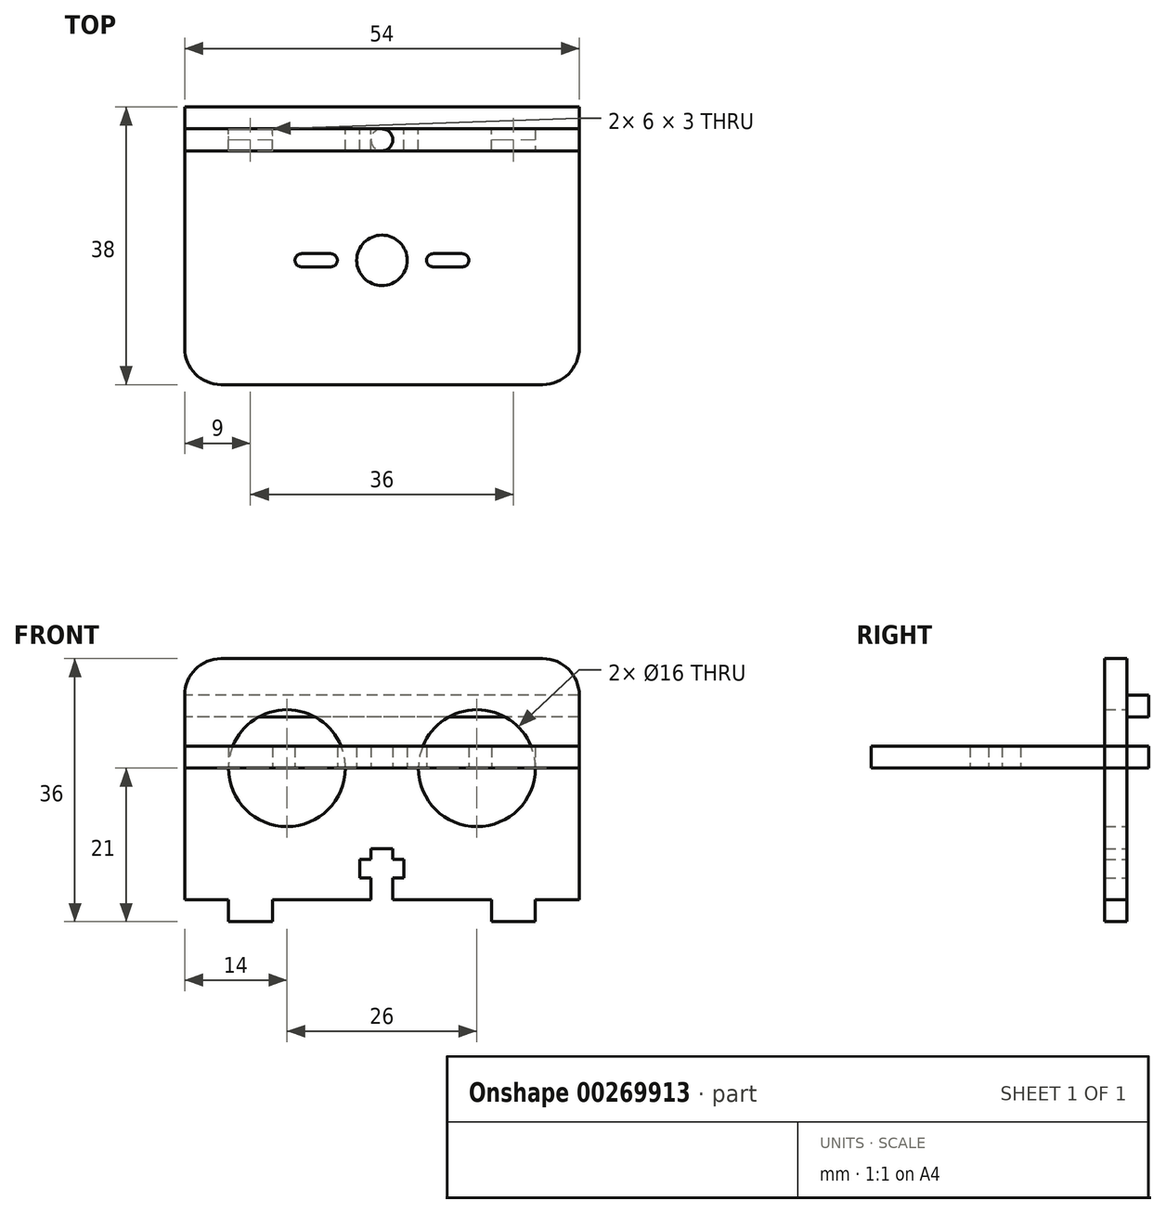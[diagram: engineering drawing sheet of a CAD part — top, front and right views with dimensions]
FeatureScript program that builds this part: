
annotation { "Feature Type Name" : "Feature", "Feature Type Description" : "" }
export const myFeature = defineFeature(function(context is Context, id is Id, definition is map)
    precondition{}
    {
        {
            var Q0;
            Q0=qCreatedBy(makeId("Front.planeOp"),FACE);
            var sketch = newSketch(context, id + "F0", { "sketchPlane" : qUnion([Q0])});
            skLineSegment(sketch, "E0.bottom", {"start": v(-22, 15) * mm, "end": v(22, 15) * mm});
            skLineSegment(sketch, "E0.left", {"start": v(-27, 10) * mm, "end": v(-27, -15) * mm});
            skLineSegment(sketch, "E0.right", {"start": v(27, 10) * mm, "end": v(27, -15) * mm});
            skCircle(sketch, "E1", {"center": v(13, 0) * mm, "radius": 8 * mm});
            skCircle(sketch, "E2", {"center": v(-13, 0) * mm, "radius": 8 * mm});
            skLineSegment(sketch, "E3", {"start": v(-36.52, -18) * mm, "end": v(-21, -18) * mm, "construction": true});
            skLineSegment(sketch, "E4", {"start": v(-9, -18) * mm, "end": v(-3, -18) * mm});
            skLineSegment(sketch, "E5", {"start": v(-3, -15) * mm, "end": v(-1.5, -15) * mm});
            skLineSegment(sketch, "E6", {"start": v(3, -18) * mm, "end": v(9, -18) * mm});
            skPoint(sketch, "E7.oppositeSnap0", {"position": v(1.5, -18) * mm});
            skLineSegment(sketch, "E7.bottom", {"start": v(0, -18) * mm, "end": v(1.5, -18) * mm});
            skLineSegment(sketch, "E7.top", {"start": v(0, -11) * mm, "end": v(1.5, -11) * mm});
            skLineSegment(sketch, "E7.right", {"start": v(1.5, -18) * mm, "end": v(1.5, -15) * mm});
            skLineSegment(sketch, "E8.trimOffspring", {"start": v(1.5, -18) * mm, "end": v(9, -18) * mm, "construction": true});
            skLineSegment(sketch, "E9", {"start": v(3, -18) * mm, "end": v(1.5, -18) * mm});
            skLineSegment(sketch, "E10.top", {"start": v(-3, -12.5) * mm, "end": v(-1.5, -12.5) * mm});
            skLineSegment(sketch, "E10.left", {"start": v(-3, -15) * mm, "end": v(-3, -12.5) * mm});
            skLineSegment(sketch, "E10.right", {"start": v(3, -15) * mm, "end": v(3, -12.5) * mm});
            skLineSegment(sketch, "E11.trimOffspring", {"start": v(1.5, -15) * mm, "end": v(3, -15) * mm});
            skLineSegment(sketch, "E12.trimOffspring", {"start": v(1.5, -12.5) * mm, "end": v(3, -12.5) * mm});
            skLineSegment(sketch, "E13", {"start": v(0, -11) * mm, "end": v(-1.5, -11) * mm});
            skLineSegment(sketch, "E14", {"start": v(-1.5, -11) * mm, "end": v(-1.5, -12.5) * mm});
            skLineSegment(sketch, "E15.trimOffspring", {"start": v(1.5, -12.5) * mm, "end": v(1.5, -11) * mm});
            skLineSegment(sketch, "E16.trimOffspring", {"start": v(-1.5, -15) * mm, "end": v(-1.5, -18) * mm});
            skLineSegment(sketch, "E17", {"start": v(-1.5, -18) * mm, "end": v(-3, -18) * mm});
            skLineSegment(sketch, "E18", {"start": v(-21, -18) * mm, "end": v(-21, -21) * mm});
            skLineSegment(sketch, "E19", {"start": v(-21, -21) * mm, "end": v(-15, -21) * mm});
            skLineSegment(sketch, "E20", {"start": v(-15, -21) * mm, "end": v(-15, -18) * mm});
            skLineSegment(sketch, "E21", {"start": v(-15, -18) * mm, "end": v(-9, -18) * mm});
            skLineSegment(sketch, "E22", {"start": v(9, -18) * mm, "end": v(15, -18) * mm});
            skLineSegment(sketch, "E23", {"start": v(15, -18) * mm, "end": v(15, -21) * mm});
            skLineSegment(sketch, "E24", {"start": v(15, -21) * mm, "end": v(21, -21) * mm});
            skLineSegment(sketch, "E25", {"start": v(21, -21) * mm, "end": v(21, -18) * mm});
            skLineSegment(sketch, "E26.trimOffspring", {"start": v(-15, -18) * mm, "end": v(0, -18) * mm, "construction": true});
            skLineSegment(sketch, "E27.trimOffspring", {"start": v(21, -18) * mm, "end": v(39.52, -18) * mm, "construction": true});
            skPoint(sketch, "E28.visualSharp", {"position": v(-27, 15) * mm});
            skArc(sketch, "E28.filletArc", {"start": v(-22, 15) * mm, "mid": v(-25.54, 13.54) * mm, "end": v(-27, 10) * mm});
            skPoint(sketch, "E29.visualSharp", {"position": v(27, 15) * mm});
            skArc(sketch, "E29.filletArc", {"start": v(27, 10) * mm, "mid": v(25.54, 13.54) * mm, "end": v(22, 15) * mm});
            skLineSegment(sketch, "E30", {"start": v(-27, -15) * mm, "end": v(-27, -18) * mm});
            skLineSegment(sketch, "E31", {"start": v(-27, -18) * mm, "end": v(-21, -18) * mm});
            skPoint(sketch, "E32.start.orphan", {"position": v(-21, -15) * mm});
            skLineSegment(sketch, "E33", {"start": v(27, -15) * mm, "end": v(27, -18) * mm});
            skLineSegment(sketch, "E34", {"start": v(27, -18) * mm, "end": v(21, -18) * mm});
            skSolve(sketch);
        }
        {
            var Q0;
            Q0=makeQuery(id+"F0.imprint","IMPRINT",FACE,{"disambiguationData":[TD([[makeQuery(id+"F0.imprint","IMPRINT",EDGE,{"derivedFrom":sQuery(id+"F0.wireOp",EDGE,"E0.bottom")}),-1.0]])]});
            var Q1;
            {var subQ0=sQuery(id+"F0.wireOp",EDGE,"E32");Q1=makeQuery(id+"F0.imprint","IMPRINT",FACE,{"disambiguationData":[TD([[makeQuery(id+"F0.imprint","IMPRINT",EDGE,{"derivedFrom":subQ0}),1.0]])]});}
            var Q2;
            {var subQ0=sQuery(id+"F0.wireOp",EDGE,"chz3AYh3-IsNQ-ujgV-jPsD-pE5skbg77R1T");Q2=makeQuery(id+"F0.imprint","IMPRINT",FACE,{"disambiguationData":[TD([[makeQuery(id+"F0.imprint","IMPRINT",EDGE,{"derivedFrom":subQ0}),1.0]])]});}
            var Q3;
            {var subQ0=sQuery(id+"F0.wireOp",EDGE,"wKKlznAo-Ev7Z-Zq9Q-11uT-MNoMT551QMHz");Q3=makeQuery(id+"F0.imprint","IMPRINT",FACE,{"disambiguationData":[TD([[makeQuery(id+"F0.imprint","IMPRINT",EDGE,{"derivedFrom":subQ0}),1.0]])]});}
            var Q4;
            {var subQ0=sQuery(id+"F0.wireOp",EDGE,"eYgF27Q2-r109-4hkZ-zSBN-Yc0fYFjueZed");Q4=makeQuery(id+"F0.imprint","IMPRINT",FACE,{"disambiguationData":[TD([[makeQuery(id+"F0.imprint","IMPRINT",EDGE,{"derivedFrom":subQ0}),1.0]])]});}
            extrude(context, id + "F1", {"entities" : qUnion([Q0, Q1, Q2, Q3, Q4]), "depth" : 3 * mm});
        }
        {
            var Q0;
            Q0=makeQuery(id+"F1.opExtrude","CAP_FACE",FACE,{"disambiguationData":[OSD([sQuery(id+"F0.wireOp",EDGE,"E0.bottom"),sQuery(id+"F0.wireOp",EDGE,"E0.top"),sQuery(id+"F0.wireOp",EDGE,"E0.left"),sQuery(id+"F0.wireOp",EDGE,"E0.right"),sQuery(id+"F0.wireOp",EDGE,"E1"),sQuery(id+"F0.wireOp",EDGE,"E2"),sQuery(id+"F0.wireOp",EDGE,"E32"),sQuery(id+"F0.wireOp",EDGE,"YojEBUgW-nhLJ-40ki-FCGF-5mKsaDnZTmev"),sQuery(id+"F0.wireOp",EDGE,"vRN4Y9O1-ZqiY-Jczt-QRZo-3q2dczrKPTGp"),sQuery(id+"F0.wireOp",EDGE,"zzXZZM5g-6FFm-bmIo-3Ds1-M5u7KWrwiJGG"),sQuery(id+"F0.wireOp",EDGE,"chz3AYh3-IsNQ-ujgV-jPsD-pE5skbg77R1T"),sQuery(id+"F0.wireOp",EDGE,"E4"),sQuery(id+"F0.wireOp",EDGE,"ghqL6N1V-hfz9-jjIh-pt2L-dAo4biIIS88P"),sQuery(id+"F0.wireOp",EDGE,"E5"),sQuery(id+"F0.wireOp",EDGE,"wKKlznAo-Ev7Z-Zq9Q-11uT-MNoMT551QMHz"),sQuery(id+"F0.wireOp",EDGE,"E6"),sQuery(id+"F0.wireOp",EDGE,"I0ca3B4m-FfYs-K0F9-6d8p-SOPzohqiJkWk"),sQuery(id+"F0.wireOp",EDGE,"1psEPeUv-bJOJ-tgm4-QE24-8bz3CrIUmwqz"),sQuery(id+"F0.wireOp",EDGE,"eYgF27Q2-r109-4hkZ-zSBN-Yc0fYFjueZed"),sQuery(id+"F0.wireOp",EDGE,"Y0FXYbVY-FO2c-i97v-nV3U-BxFzxJudH6SC"),sQuery(id+"F0.wireOp",EDGE,"8HbA60u2-9wGZ-Dvxy-T3Xx-RcAAK77T48SR")])],"isStart":true});
            var sketch = newSketch(context, id + "F2", { "sketchPlane" : qUnion([Q0])});
            skLineSegment(sketch, "E35.bottom", {"start": v(-27, 10) * mm, "end": v(27, 10) * mm});
            skLineSegment(sketch, "E35.top", {"start": v(-27, 7) * mm, "end": v(27, 7) * mm});
            skLineSegment(sketch, "E35.left", {"start": v(-27, 10) * mm, "end": v(-27, 7) * mm});
            skLineSegment(sketch, "E35.right", {"start": v(27, 10) * mm, "end": v(27, 7) * mm});
            skSolve(sketch);
        }
        {
            var Q0;
            Q0 = qSketchRegion(id + "F2", true);
            extrude(context, id + "F3", {"entities" : qUnion([Q0]), "depth" : 3 * mm, "offsetDistance" : 25 * mm});
        }
        {
            var Q0;
            Q0=qCreatedBy(makeId("Top.planeOp"),FACE);
            var sketch = newSketch(context, id + "F4", { "sketchPlane" : qUnion([Q0])});
            skLineSegment(sketch, "E36.0", {"start": v(-27, -3) * mm, "end": v(-27, 0) * mm});
            skLineSegment(sketch, "E37.0", {"start": v(27, 0) * mm, "end": v(27, -3) * mm});
            skLineSegment(sketch, "E38.top", {"start": v(-21, 0) * mm, "end": v(-15, 0) * mm});
            skLineSegment(sketch, "E38.left", {"start": v(-27, 0) * mm, "end": v(-27, 0) * mm});
            skLineSegment(sketch, "E38.right", {"start": v(27, 0) * mm, "end": v(27, 0) * mm});
            skLineSegment(sketch, "E39.top", {"start": v(-22, -35) * mm, "end": v(22, -35) * mm});
            skLineSegment(sketch, "E39.left", {"start": v(-27, 0) * mm, "end": v(-27, -30) * mm});
            skLineSegment(sketch, "E39.right", {"start": v(27, 0) * mm, "end": v(27, -30) * mm});
            skLineSegment(sketch, "E40", {"start": v(-29.98, -1.5) * mm, "end": v(31.4, -1.5) * mm, "construction": true});
            skCircle(sketch, "E41", {"center": v(0, -1.5) * mm, "radius": 1.5 * mm});
            skLineSegment(sketch, "E42", {"start": v(-27, -3) * mm, "end": v(27, -3) * mm, "construction": true});
            skLineSegment(sketch, "E43.0", {"start": v(-21, -3) * mm, "end": v(-21, 0) * mm});
            skLineSegment(sketch, "E44.0", {"start": v(-15, -3) * mm, "end": v(-15, 0) * mm});
            skLineSegment(sketch, "E45.0", {"start": v(15, -3) * mm, "end": v(15, 0) * mm});
            skLineSegment(sketch, "E46.0", {"start": v(21, 0) * mm, "end": v(21, -3) * mm});
            skLineSegment(sketch, "E47.bottom", {"start": v(-21, -3) * mm, "end": v(-15, -3) * mm, "construction": true});
            skLineSegment(sketch, "E47.top", {"start": v(-21, 0) * mm, "end": v(-15, 0) * mm, "construction": true});
            skLineSegment(sketch, "E47.left", {"start": v(-21, -3) * mm, "end": v(-21, 0) * mm, "construction": true});
            skLineSegment(sketch, "E47.right", {"start": v(-15, -3) * mm, "end": v(-15, 0) * mm, "construction": true});
            skLineSegment(sketch, "E48.bottom", {"start": v(15, -3) * mm, "end": v(21, -3) * mm, "construction": true});
            skLineSegment(sketch, "E48.top", {"start": v(15, 0) * mm, "end": v(21, 0) * mm, "construction": true});
            skLineSegment(sketch, "E48.left", {"start": v(15, -3) * mm, "end": v(15, 0) * mm, "construction": true});
            skLineSegment(sketch, "E48.right", {"start": v(21, -3) * mm, "end": v(21, 0) * mm, "construction": true});
            skLineSegment(sketch, "E49", {"start": v(27, 0) * mm, "end": v(27, 3) * mm});
            skLineSegment(sketch, "E50", {"start": v(27, 3) * mm, "end": v(-27, 3) * mm});
            skLineSegment(sketch, "E51", {"start": v(-27, 3) * mm, "end": v(-27, 0) * mm});
            skLineSegment(sketch, "E52.trimOffspring", {"start": v(0, 0) * mm, "end": v(21, 0) * mm});
            skLineSegment(sketch, "E53.trimOffspring", {"start": v(15, 0) * mm, "end": v(21, 0) * mm});
            skLineSegment(sketch, "E54", {"start": v(-21, -3) * mm, "end": v(-15, -3) * mm});
            skLineSegment(sketch, "E55", {"start": v(15, -3) * mm, "end": v(21, -3) * mm});
            skPoint(sketch, "E56", {"position": v(0, -17.98) * mm});
            skCircle(sketch, "E57", {"center": v(0, -17.98) * mm, "radius": 3.45 * mm});
            skArc(sketch, "E58", {"start": v(11, -18.88) * mm, "mid": v(11.9, -17.98) * mm, "end": v(11, -17.08) * mm});
            skArc(sketch, "E59", {"start": v(7, -17.08) * mm, "mid": v(6.1, -17.98) * mm, "end": v(7, -18.88) * mm});
            skArc(sketch, "E60.MirrorC", {"start": v(-11, -18.88) * mm, "mid": v(-11.9, -17.98) * mm, "end": v(-11, -17.08) * mm});
            skArc(sketch, "E61.MirrorC", {"start": v(-7, -17.08) * mm, "mid": v(-6.1, -17.98) * mm, "end": v(-7, -18.88) * mm});
            skLineSegment(sketch, "E62", {"start": v(0, -1.5) * mm, "end": v(0, -37.31) * mm, "construction": true});
            skLineSegment(sketch, "E63", {"start": v(-11, -18.88) * mm, "end": v(-7, -18.88) * mm});
            skLineSegment(sketch, "E64", {"start": v(-11, -17.08) * mm, "end": v(-7, -17.08) * mm});
            skLineSegment(sketch, "E65", {"start": v(7, -18.88) * mm, "end": v(11, -18.88) * mm});
            skLineSegment(sketch, "E66", {"start": v(11, -17.08) * mm, "end": v(7, -17.08) * mm});
            skPoint(sketch, "E67.visualSharp", {"position": v(-27, -35) * mm});
            skArc(sketch, "E67.filletArc", {"start": v(-27, -30) * mm, "mid": v(-25.54, -33.54) * mm, "end": v(-22, -35) * mm});
            skPoint(sketch, "E68.visualSharp", {"position": v(27, -35) * mm});
            skArc(sketch, "E68.filletArc", {"start": v(22, -35) * mm, "mid": v(25.54, -33.54) * mm, "end": v(27, -30) * mm});
            skSolve(sketch);
        }
        {
            var Q0;
            Q0=makeQuery(id+"F4.imprint","IMPRINT",FACE,{"disambiguationData":[TD([[makeQuery(id+"F4.imprint","IMPRINT",EDGE,{"derivedFrom":sQuery(id+"F4.wireOp",EDGE,"E38.top")}),1.0]])]});
            extrude(context, id + "F5", {"entities" : qUnion([Q0]), "depth" : 3 * mm, "offsetDistance" : 25 * mm});
        }
    });
